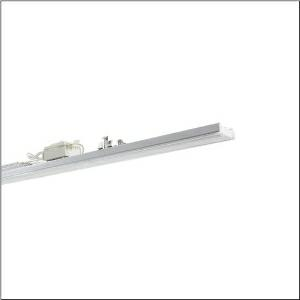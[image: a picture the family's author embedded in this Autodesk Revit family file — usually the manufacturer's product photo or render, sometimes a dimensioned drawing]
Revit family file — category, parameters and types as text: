
# Revit family: licross_11_recessed_mo_51te10cn49xg
name_source: partatom
category: Lighting Fixtures
units: mm (PartAtom-declared; Revit-internal decimal feet)

## family parameters
Cut with Voids When Loaded = No
Host = Face
Light Source = No
Part Type = Normal
Room Calculation Point = No
Round Connector Dimension = Use Diameter
Shared = No

## types (1)
- --- (1 x LED, 9050 lm, 49.3 W, 4000K)
    Apparent Load = 49 VA
    CIE Flux Codes = 50 81 96 100 100
    Color Rendering = 80
    Color Temperature = 4000K
    Default Elevation = 1800 mm
    Description = Licross 11 Recessed MO, luminaire insert, of sheet steel, galvanised, coil coated, white, length: 1.500mm, width: 66mm, height: 67mm, LED rated luminous flux: 9.050lm, light colour: 840, SDCM (Standard Deviation of Colour Matching)MacAdam ≤ 2 SDCM (initial), control gear: ON/OFF Multilumen, CLOi, with plug, 3-pole, with phase selection, mains connection: 220..240V, AC, 50/60Hz, start of lifetime: 49W, end of service life: 55W, internal wiring halogen-free, primary optical cover: cover, of PMMA, light emission: direct distribution, primary light characteristic: symmetric, protection rating (complete): IP54, insulation class (complete): insulation class I (protective earthing), certification: CE, ENEC, VDE, UKCA, protection symbol: D if used in an environment with non-conductive dust loads with corresponding accessories, impact resistance: IK06, permissible ambient temperature for indoor applications: -35..+40°C, corresponds to IFS (International Featured Standards) requirements for safety and quality in the food industry, reducing of maximum allowable ambient temperature of 5°C with ceiling mounting, LABS conformity tested according to VDMA 24364:2018-05, The light source and the operating device comply with the requirements of the Ecodesign Regulation (EU) 2019/2020 and are replaceable in accordance with this regulation, packaging unit: 1 piece
    Height = 58 mm
    Lamp = 1 x LED
    Lamp Light Flux = 9050 lm
    Lamp Power = 49.3 W
    Lamp count = 1
    Length = 1500 mm
    Luminous efficacy = 184 lm/W
    Manufacturer = Siteco
    ModVariant = No
    Model = 51TE10CN49XG
    Mounting Place = Ceiling
    Mounting Type = Pendant
    Number of Poles = 1
    OnlyDefault = Yes
    Power Factor = 1
    Product Name = Licross 11 Recessed MO
    Product group = luminaire insert | ceiling pendant
    ProductGroupID = 901
    Protection Class = Protection class I
    Protection Degree = IP 54
    RLX_Detail_Level = 1
    RLX_Emergency_Light_Flux = 0 lm
    RLX_Emergency_Type = 0
    RLX_Emergency_Type_DB = No
    RlxData = <blob elided: 22485 chars, md5=4df5b74e>
    Socket = socket
    Standby Power = 0 W
    System Light Flux = 9050 lm
    System Power = 49 W
    Type Comments = factory setting: luminous flux: 100 % | (A | C | E) | 113 mA
    Type Image = l_1296930.jpg
    URL = http://relux.com
    VarID = @adj_090483
    Voltage = 0 V
    Weight = 0.00 kg
    Width = 66 mm

## geometry (parser evidence)
native form markers: Blend x4, Sweep x11
no freeform markers — native parametric forms only
